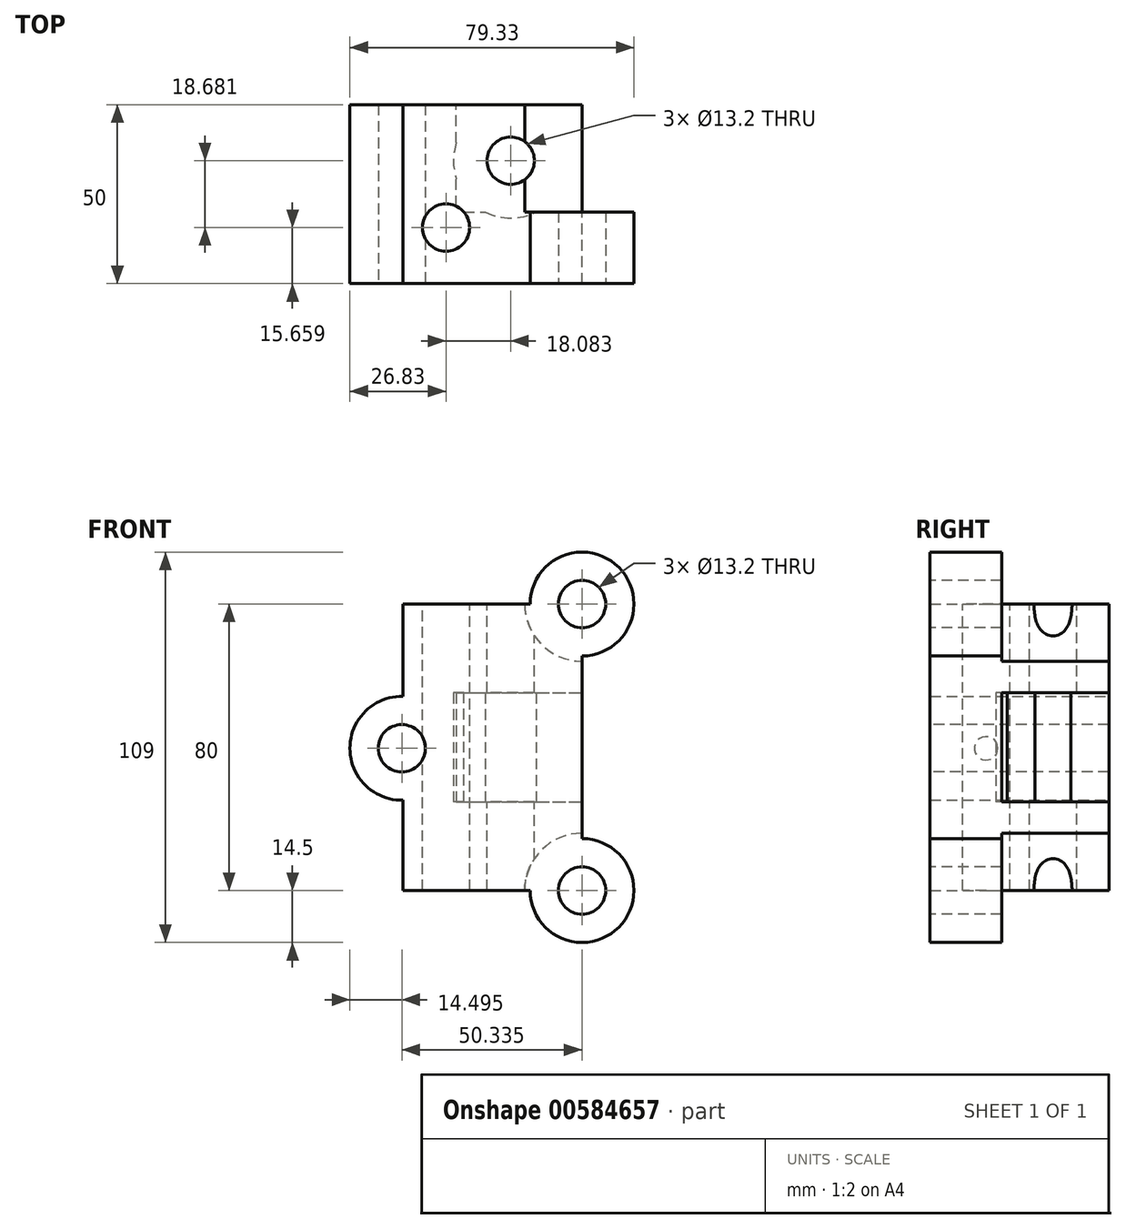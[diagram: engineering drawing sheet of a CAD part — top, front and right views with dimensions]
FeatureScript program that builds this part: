
annotation { "Feature Type Name" : "Feature", "Feature Type Description" : "" }
export const myFeature = defineFeature(function(context is Context, id is Id, definition is map)
    precondition{}
    {
        {
            var Q0;
            Q0=qCreatedBy(makeId("Front.planeOp"),FACE);
            var sketch = newSketch(context, id + "F0", { "sketchPlane" : qUnion([Q0])});
            skLineSegment(sketch, "E0.bottom", {"start": v(25, -40) * mm, "end": v(-25, -40) * mm});
            skLineSegment(sketch, "E0.top", {"start": v(25, 40) * mm, "end": v(-25, 40) * mm});
            skLineSegment(sketch, "E0.left", {"start": v(25, -40) * mm, "end": v(25, 40) * mm});
            skLineSegment(sketch, "E0.right", {"start": v(-25, -40) * mm, "end": v(-25, 40) * mm});
            skPoint(sketch, "E0.middle", {"position": v(0, 0) * mm});
            skCircle(sketch, "E1", {"center": v(25, 40) * mm, "radius": 14.5 * mm});
            skCircle(sketch, "E2", {"center": v(25, -40) * mm, "radius": 14.5 * mm});
            skCircle(sketch, "E3", {"center": v(-25.33, -0.28) * mm, "radius": 14.5 * mm});
            skSolve(sketch);
        }
        {
            var Q0;
            Q0=qSketchRegion(id+"F0",true);
            extrude(context, id + "F1", {"entities" : qUnion([Q0]), "endBound" : BoundingType.SYMMETRIC, "depth" : 50 * mm, "offsetDistance" : 25 * mm});
        }
        {
            var Q0;
            Q0=makeQuery(id+"F1.opExtrude","CAP_FACE",FACE,{"disambiguationData":[OSD([sQuery(id+"F0.wireOp",EDGE,"E0.bottom"),sQuery(id+"F0.wireOp",EDGE,"E0.top"),sQuery(id+"F0.wireOp",EDGE,"E0.left"),sQuery(id+"F0.wireOp",EDGE,"E0.right"),sQuery(id+"F0.wireOp",EDGE,"E1"),sQuery(id+"F0.wireOp",EDGE,"E2"),sQuery(id+"F0.wireOp",EDGE,"E3")])],"isStart":false});
            var sketch = newSketch(context, id + "F2", { "sketchPlane" : qUnion([Q0])});
            skPoint(sketch, "E4", {"position": v(25, 40) * mm});
            skPoint(sketch, "E5", {"position": v(25, -40) * mm});
            skPoint(sketch, "E6", {"position": v(-25.33, -0.28) * mm});
            skSolve(sketch);
        }
        {
            var Q0;
            Q0=sQuery(id+"F2.wireOp",VERTEX,"E4");
            var Q1;
            Q1=sQuery(id+"F2.wireOp",VERTEX,"E6");
            var Q2;
            Q2=sQuery(id+"F2.wireOp",VERTEX,"E5");
            var Q3;
            Q3=makeQuery(id+"F1.opExtrude","SWEPT_BODY",BODY,{"disambiguationData":[OSD([sQuery(id+"F0.wireOp",EDGE,"E0.bottom"),sQuery(id+"F0.wireOp",EDGE,"E0.top"),sQuery(id+"F0.wireOp",EDGE,"E0.left"),sQuery(id+"F0.wireOp",EDGE,"E0.right"),sQuery(id+"F0.wireOp",EDGE,"E1"),sQuery(id+"F0.wireOp",EDGE,"E2"),sQuery(id+"F0.wireOp",EDGE,"E3")])]});
            hole(context, id + "F3", {"style" : HoleStyle.C_BORE, "endStyle" : HoleEndStyle.THROUGH, "holeDiameter" : 13.2 * mm, "cBoreDiameter" : 19.25 * mm, "cBoreDepth" : 0 * mm, "majorDiameter" : 5 * mm, "isTappedThrough" : true, "tappedDepth" : 12 * mm, "tapClearance" : 3, "startFromSketch" : true, "locations" : qUnion([Q0, Q1, Q2]), "scope" : qUnion([Q3])});
        }
        {
            var Q0;
            Q0=makeQuery(id+"F1.opExtrude","SWEPT_FACE",FACE,{"disambiguationData":[OSD([sQuery(id+"F0.wireOp",EDGE,"E0.top")])]});
            var sketch = newSketch(context, id + "F4", { "sketchPlane" : qUnion([Q0])});
            skLineSegment(sketch, "E7.bottom", {"start": v(5.08, 9.34) * mm, "end": v(-13, 9.34) * mm});
            skLineSegment(sketch, "E7.top", {"start": v(5.08, -9.34) * mm, "end": v(-13, -9.34) * mm});
            skLineSegment(sketch, "E7.left", {"start": v(-13, -9.34) * mm, "end": v(-13, 9.34) * mm});
            skLineSegment(sketch, "E7.right", {"start": v(5.08, -9.34) * mm, "end": v(5.08, 9.34) * mm});
            skPoint(sketch, "E8", {"position": v(5.08, 9.34) * mm});
            skPoint(sketch, "E9", {"position": v(-13, -9.34) * mm});
            skSolve(sketch);
        }
        {
            var Q0;
            Q0=sQuery(id+"F4.wireOp",VERTEX,"E9");
            var Q1;
            Q1=sQuery(id+"F4.wireOp",VERTEX,"E8");
            var Q2;
            Q2=makeQuery(id+"F1.opExtrude","SWEPT_BODY",BODY,{"disambiguationData":[OSD([sQuery(id+"F0.wireOp",EDGE,"E0.bottom"),sQuery(id+"F0.wireOp",EDGE,"E0.top"),sQuery(id+"F0.wireOp",EDGE,"E0.left"),sQuery(id+"F0.wireOp",EDGE,"E0.right"),sQuery(id+"F0.wireOp",EDGE,"E1"),sQuery(id+"F0.wireOp",EDGE,"E2"),sQuery(id+"F0.wireOp",EDGE,"E3")])]});
            hole(context, id + "F5", {"style" : HoleStyle.C_BORE, "endStyle" : HoleEndStyle.THROUGH, "holeDiameter" : 13.2 * mm, "cBoreDiameter" : 19.25 * mm, "cBoreDepth" : 0 * mm, "majorDiameter" : 5 * mm, "isTappedThrough" : true, "tappedDepth" : 12 * mm, "tapClearance" : 3, "startFromSketch" : true, "locations" : qUnion([Q0, Q1]), "scope" : qUnion([Q2])});
        }
        {
            var Q0;
            Q0=makeQuery(id+"F1.opExtrude","CAP_FACE",FACE,{"disambiguationData":[OSD([sQuery(id+"F0.wireOp",EDGE,"E0.bottom"),sQuery(id+"F0.wireOp",EDGE,"E0.top"),sQuery(id+"F0.wireOp",EDGE,"E0.left"),sQuery(id+"F0.wireOp",EDGE,"E0.right"),sQuery(id+"F0.wireOp",EDGE,"E1"),sQuery(id+"F0.wireOp",EDGE,"E2"),sQuery(id+"F0.wireOp",EDGE,"E3")])],"isStart":true});
            var sketch = newSketch(context, id + "F6", { "sketchPlane" : qUnion([Q0])});
            skLineSegment(sketch, "E10.bottom", {"start": v(10.1, 15.25) * mm, "end": v(-29.9, 15.25) * mm});
            skLineSegment(sketch, "E10.top", {"start": v(10.1, -15.25) * mm, "end": v(-29.9, -15.25) * mm});
            skLineSegment(sketch, "E10.left", {"start": v(10.1, 15.25) * mm, "end": v(10.1, -15.25) * mm});
            skLineSegment(sketch, "E10.right", {"start": v(-29.9, 15.25) * mm, "end": v(-29.9, -15.25) * mm});
            skPoint(sketch, "E10.middle", {"position": v(-9.9, 0) * mm});
            skSolve(sketch);
        }
        {
            var Q0;
            Q0 = qSketchRegion(id + "F6", true);
            extrude(context, id + "F7", {"entities" : qUnion([Q0]), "operationType" : NewBodyOperationType.REMOVE, "oppositeDirection" : true, "depth" : 30 * mm, "offsetDistance" : 25 * mm});
        }
        {
            var Q0;
            Q0=makeQuery(id+"F7.boolean.opBoolean","COPY",FACE,{"derivedFrom":makeQuery(id+"F7.opExtrude","SWEPT_FACE",FACE,{"disambiguationData":[OSD([sQuery(id+"F6.wireOp",EDGE,"E10.top")])]})});
            var sketch = newSketch(context, id + "F8", { "sketchPlane" : qUnion([Q0])});
            skCircle(sketch, "E11", {"center": v(5.08, 9.34) * mm, "radius": 16 * mm});
            skSolve(sketch);
        }
        {
            var Q0;
            Q0 = qSketchRegion(id + "F8", true);
            extrude(context, id + "F9", {"entities" : qUnion([Q0]), "operationType" : NewBodyOperationType.REMOVE, "oppositeDirection" : true, "depth" : -30.5 * mm, "offsetDistance" : 25 * mm});
        }
        {
            var Q0;
            Q0=makeQuery(id+"F1.opExtrude","CAP_FACE",FACE,{"disambiguationData":[OSD([sQuery(id+"F0.wireOp",EDGE,"E0.bottom"),sQuery(id+"F0.wireOp",EDGE,"E0.top"),sQuery(id+"F0.wireOp",EDGE,"E0.left"),sQuery(id+"F0.wireOp",EDGE,"E0.right"),sQuery(id+"F0.wireOp",EDGE,"E1"),sQuery(id+"F0.wireOp",EDGE,"E2"),sQuery(id+"F0.wireOp",EDGE,"E3")])],"isStart":true});
            var sketch = newSketch(context, id + "F10", { "sketchPlane" : qUnion([Q0])});
            skCircle(sketch, "E12", {"center": v(-25, 40) * mm, "radius": 16 * mm});
            skCircle(sketch, "E13", {"center": v(-25, -40) * mm, "radius": 16 * mm});
            skSolve(sketch);
        }
        {
            var Q0;
            Q0 = qSketchRegion(id + "F10", true);
            extrude(context, id + "F11", {"entities" : qUnion([Q0]), "operationType" : NewBodyOperationType.REMOVE, "oppositeDirection" : true, "depth" : 30 * mm, "offsetDistance" : 25 * mm});
        }
    });
